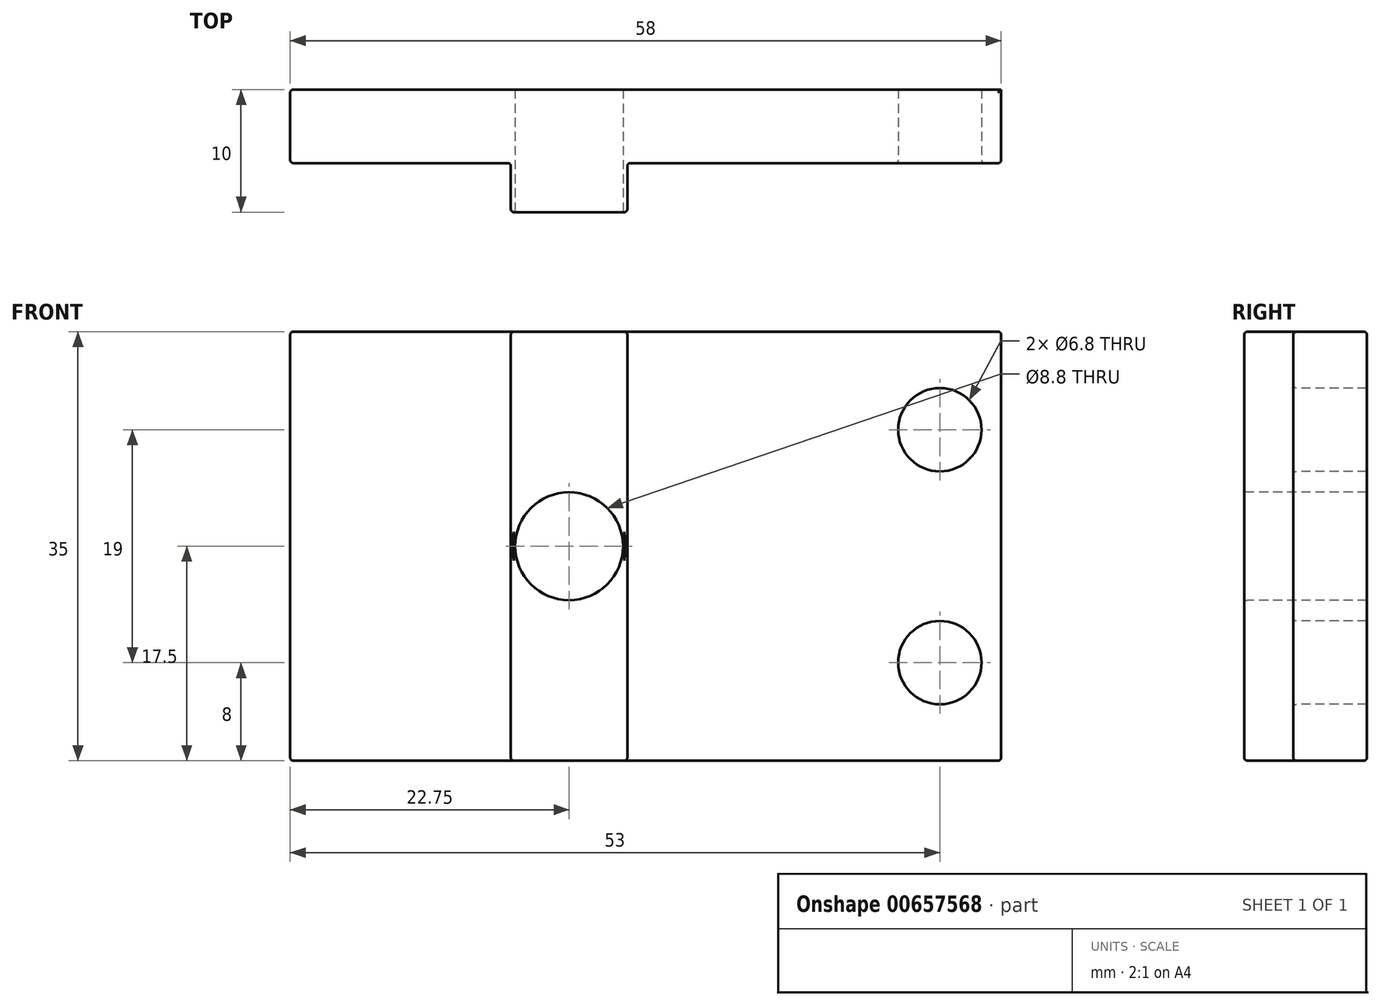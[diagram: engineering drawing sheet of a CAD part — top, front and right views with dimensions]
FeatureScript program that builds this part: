
annotation { "Feature Type Name" : "Feature", "Feature Type Description" : "" }
export const myFeature = defineFeature(function(context is Context, id is Id, definition is map)
    precondition{}
    {
        {
            var Q0;
            Q0=qCreatedBy(makeId("Front.planeOp"),FACE);
            var sketch = newSketch(context, id + "F0", { "sketchPlane" : qUnion([Q0])});
            skLineSegment(sketch, "E0.bottom", {"start": v(29, 17.5) * mm, "end": v(-29, 17.5) * mm});
            skLineSegment(sketch, "E0.top", {"start": v(29, -17.5) * mm, "end": v(-29, -17.5) * mm});
            skLineSegment(sketch, "E0.left", {"start": v(29, 17.5) * mm, "end": v(29, -17.5) * mm});
            skLineSegment(sketch, "E0.right", {"start": v(-29, 17.5) * mm, "end": v(-29, -17.5) * mm});
            skPoint(sketch, "E0.middle", {"position": v(0, 0) * mm});
            skSolve(sketch);
        }
        {
            var Q0;
            Q0=makeQuery(id+"F0.imprint","IMPRINT",FACE,{"disambiguationData":[TD([[makeQuery(id+"F0.imprint","IMPRINT",EDGE,{"derivedFrom":sQuery(id+"F0.wireOp",EDGE,"E0.bottom")}),1.0]])]});
            extrude(context, id + "F1", {"entities" : qUnion([Q0]), "depth" : 6 * mm, "offsetDistance" : 25 * mm});
        }
        {
            var Q0;
            Q0=makeQuery(id+"F1.opExtrude","CAP_FACE",FACE,{"disambiguationData":[OSD([sQuery(id+"F0.wireOp",EDGE,"E0.bottom"),sQuery(id+"F0.wireOp",EDGE,"E0.top"),sQuery(id+"F0.wireOp",EDGE,"E0.left"),sQuery(id+"F0.wireOp",EDGE,"E0.right")])],"isStart":false});
            var sketch = newSketch(context, id + "F2", { "sketchPlane" : qUnion([Q0])});
            skPoint(sketch, "E1", {"position": v(-6.5, 0) * mm});
            skPoint(sketch, "E2", {"position": v(-11, -17.5) * mm});
            skLineSegment(sketch, "E3", {"start": v(-11, -17.5) * mm, "end": v(-11, 17.5) * mm});
            skLineSegment(sketch, "E4", {"start": v(-11, 17.5) * mm, "end": v(-1.5, 17.5) * mm});
            skLineSegment(sketch, "E5", {"start": v(-1.5, -17.5) * mm, "end": v(-1.5, 17.5) * mm});
            skLineSegment(sketch, "E6", {"start": v(-1.5, -17.5) * mm, "end": v(-11, -17.5) * mm});
            skPoint(sketch, "E7", {"position": v(24, 9.5) * mm});
            skPoint(sketch, "E8", {"position": v(24, -9.5) * mm});
            skSolve(sketch);
        }
        {
            var Q0;
            Q0=makeQuery(id+"F2.imprint","IMPRINT",FACE,{"disambiguationData":[TD([[makeQuery(id+"F2.imprint","IMPRINT",EDGE,{"derivedFrom":sQuery(id+"F2.wireOp",EDGE,"E3")}),-1.0]])]});
            extrude(context, id + "F3", {"entities" : qUnion([Q0]), "operationType" : NewBodyOperationType.ADD, "depth" : 4 * mm, "offsetDistance" : 25 * mm});
        }
        {
            var Q0;
            Q0=sQuery(id+"F2.wireOp",VERTEX,"E7");
            var Q1;
            Q1=sQuery(id+"F2.wireOp",VERTEX,"E8");
            var Q2;
            Q2=makeQuery(id+"F1.opExtrude","SWEPT_BODY",BODY,{"disambiguationData":[OSD([sQuery(id+"F0.wireOp",EDGE,"E0.bottom"),sQuery(id+"F0.wireOp",EDGE,"E0.top"),sQuery(id+"F0.wireOp",EDGE,"E0.left"),sQuery(id+"F0.wireOp",EDGE,"E0.right")])]});
            hole(context, id + "F4", {"style" : HoleStyle.SIMPLE, "endStyle" : HoleEndStyle.THROUGH, "standardTappedOrClearance" : lookupTablePath({ "standard" : "ISO", "engagement" : "75%", "pitch" : "1.25 mm", "size" : "M8", "type" : "Tapped" }), "standardBlindInLast" : lookupTablePath({ "standard" : "ISO", "engagement" : "75%", "pitch" : "1.25 mm", "size" : "M8", "type" : "Tapped" }), "holeDiameter" : 6.8 * mm, "majorDiameter" : 8 * mm, "showTappedDepth" : true, "isTappedThrough" : true, "tappedDepth" : 19 * mm, "tapClearance" : 3, "startFromSketch" : true, "locations" : qUnion([Q0, Q1]), "scope" : qUnion([Q2])});
        }
        {
            var Q0;
            Q0=makeQuery(id+"F3.opExtrude","CAP_FACE",FACE,{"disambiguationData":[OSD([sQuery(id+"F2.wireOp",EDGE,"E3"),sQuery(id+"F2.wireOp",EDGE,"E4"),sQuery(id+"F2.wireOp",EDGE,"E5"),sQuery(id+"F2.wireOp",EDGE,"E6")])],"isStart":false});
            var sketch = newSketch(context, id + "F5", { "sketchPlane" : qUnion([Q0])});
            skPoint(sketch, "E9", {"position": v(-6.25, 0) * mm});
            skPoint(sketch, "E9.positionSnap0", {"position": v(-6.25, -17.5) * mm});
            skSolve(sketch);
        }
        {
            var Q0;
            Q0=sQuery(id+"F5.wireOp",VERTEX,"E9");
            var Q1;
            Q1=makeQuery(id+"F1.opExtrude","SWEPT_BODY",BODY,{"disambiguationData":[OSD([sQuery(id+"F0.wireOp",EDGE,"E0.bottom"),sQuery(id+"F0.wireOp",EDGE,"E0.top"),sQuery(id+"F0.wireOp",EDGE,"E0.left"),sQuery(id+"F0.wireOp",EDGE,"E0.right")])]});
            hole(context, id + "F6", {"style" : HoleStyle.SIMPLE, "endStyle" : HoleEndStyle.THROUGH, "standardTappedOrClearance" : lookupTablePath({ "standard" : "ISO", "fit" : "Normal", "size" : "M8", "type" : "Clearance" }), "standardBlindInLast" : lookupTablePath({ "fit" : "Standard", "standard" : "ISO", "size" : "M8", "type" : "Clearance" }), "holeDiameter" : 8.8 * mm, "majorDiameter" : 8 * mm, "isTappedThrough" : true, "tappedDepth" : 19 * mm, "tapClearance" : 3, "startFromSketch" : true, "locations" : qUnion([Q0]), "scope" : qUnion([Q1])});
        }
        {
            var Q0;
            {var subQ0=sQuery(id+"F0.wireOp",EDGE,"E0.left");var subQ1=sQuery(id+"F0.wireOp",EDGE,"E0.top");var subQ2=sQuery(id+"F0.wireOp",EDGE,"E0.bottom");Q0=makeQuery(id+"F3.boolean.opBoolean","SPLIT",FACE,{"disambiguationData":[TD([makeQuery(id+"F1.opExtrude","SWEPT_FACE",FACE,{"disambiguationData":[OSD([subQ0])]})])],"derivedFrom":makeQuery(id+"F1.opExtrude","CAP_FACE",FACE,{"disambiguationData":[OSD([subQ2,subQ1,subQ0,sQuery(id+"F0.wireOp",EDGE,"E0.right")])],"isStart":false})});}
            var Q1;
            Q1=makeQuery(id+"F3.opExtrude","CAP_FACE",FACE,{"disambiguationData":[OSD([sQuery(id+"F2.wireOp",EDGE,"E3"),sQuery(id+"F2.wireOp",EDGE,"E4"),sQuery(id+"F2.wireOp",EDGE,"E5"),sQuery(id+"F2.wireOp",EDGE,"E6")])],"isStart":false});
            var Q2;
            {var subQ0=sQuery(id+"F0.wireOp",EDGE,"E0.top");var subQ1=sQuery(id+"F0.wireOp",EDGE,"E0.right");var subQ2=sQuery(id+"F0.wireOp",EDGE,"E0.bottom");Q2=makeQuery(id+"F3.boolean.opBoolean","SPLIT",FACE,{"disambiguationData":[TD([makeQuery(id+"F1.opExtrude","SWEPT_FACE",FACE,{"disambiguationData":[OSD([subQ1])]})])],"derivedFrom":makeQuery(id+"F1.opExtrude","CAP_FACE",FACE,{"disambiguationData":[OSD([subQ2,subQ0,sQuery(id+"F0.wireOp",EDGE,"E0.left"),subQ1])],"isStart":false})});}
            var Q3;
            Q3=makeQuery(id+"F3.boolean.opBoolean","MERGE",FACE,{"derivedFrom":[makeQuery(id+"F1.opExtrude","SWEPT_FACE",FACE,{"disambiguationData":[OSD([sQuery(id+"F0.wireOp",EDGE,"E0.bottom")])]}),makeQuery(id+"F3.opExtrude","SWEPT_FACE",FACE,{"disambiguationData":[OSD([sQuery(id+"F2.wireOp",EDGE,"E4")])]})]});
            var Q4;
            Q4=makeQuery(id+"F1.opExtrude","CAP_EDGE",EDGE,{"disambiguationData":[OSD([sQuery(id+"F0.wireOp",EDGE,"E0.right")])],"isStart":true});
            var Q5;
            Q5=makeQuery(id+"F3.boolean.opBoolean","MERGE",FACE,{"derivedFrom":[makeQuery(id+"F1.opExtrude","SWEPT_FACE",FACE,{"disambiguationData":[OSD([sQuery(id+"F0.wireOp",EDGE,"E0.top")])]}),makeQuery(id+"F3.opExtrude","SWEPT_FACE",FACE,{"disambiguationData":[OSD([sQuery(id+"F2.wireOp",EDGE,"E6")])]})]});
            fillet(context, id + "F7", {"entities" : qUnion([Q0, Q1, Q2, Q3, Q4, Q5]), "radius" : .25 * mm, "tangentPropagation" : true, "allowEdgeOverflow" : false});
        }
    });
